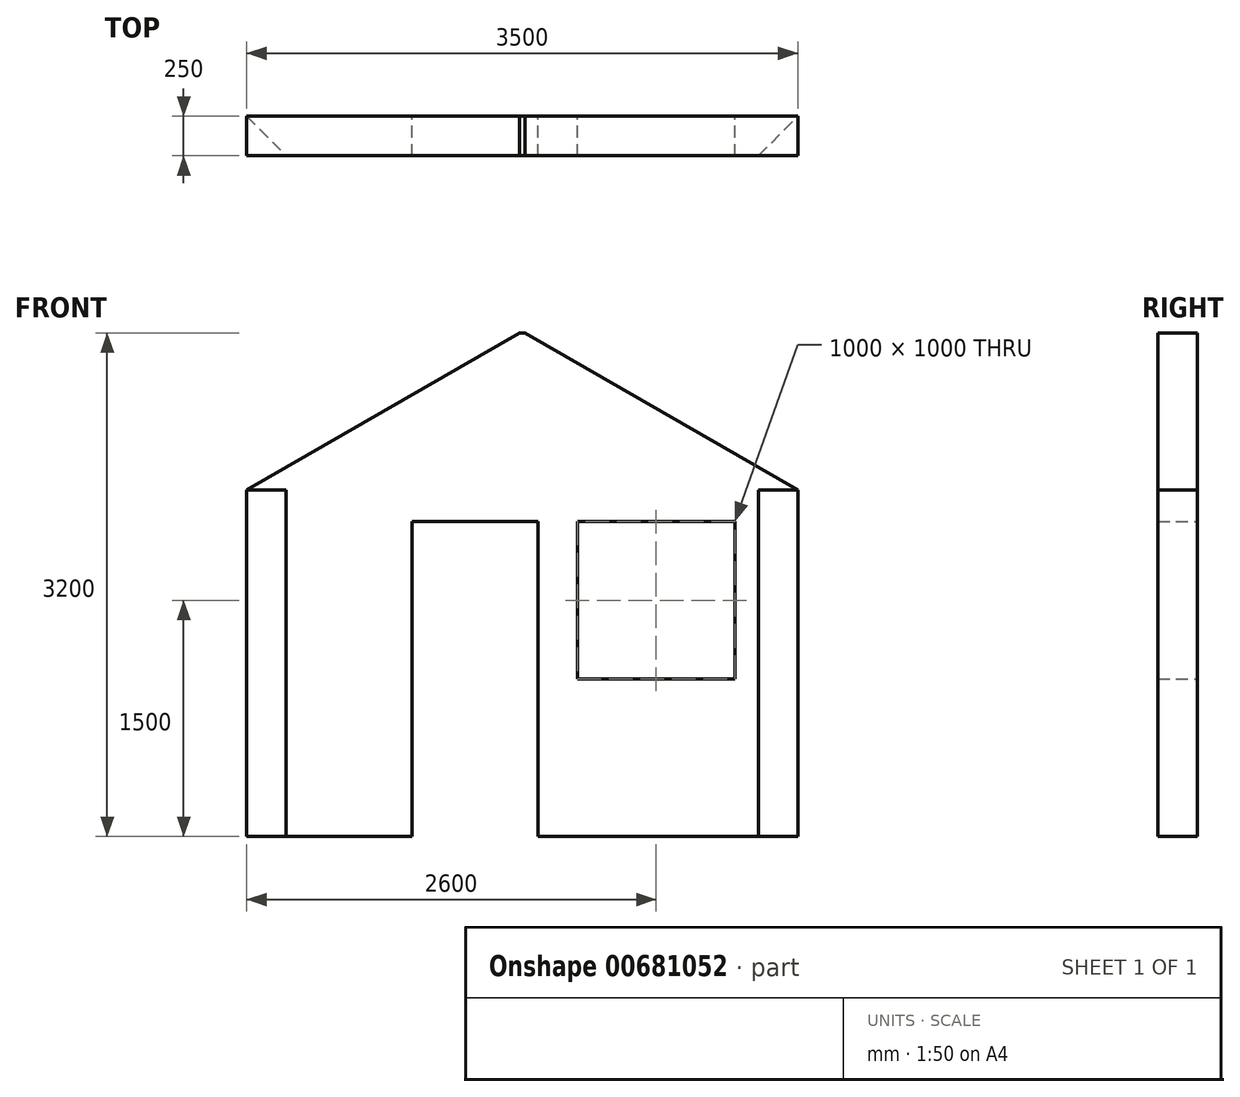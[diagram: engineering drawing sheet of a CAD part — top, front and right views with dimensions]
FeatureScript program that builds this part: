
annotation { "Feature Type Name" : "Feature", "Feature Type Description" : "" }
export const myFeature = defineFeature(function(context is Context, id is Id, definition is map)
    precondition{}
    {
        {
            var Q0;
            Q0=qCreatedBy(makeId("Front.planeOp"),FACE);
            var sketch = newSketch(context, id + "F0", { "sketchPlane" : qUnion([Q0])});
            skLineSegment(sketch, "E0.bottom", {"start": v(0, 0) * mm, "end": v(3500, 0) * mm});
            skLineSegment(sketch, "E0.top", {"start": v(0, 2200) * mm, "end": v(3500, 2200) * mm});
            skLineSegment(sketch, "E0.left", {"start": v(0, 0) * mm, "end": v(0, 2200) * mm});
            skLineSegment(sketch, "E0.right", {"start": v(3500, 0) * mm, "end": v(3500, 2200) * mm});
            skSolve(sketch);
        }
        {
            var Q0;
            Q0=qSketchRegion(id+"F0",true);
            extrude(context, id + "F1", {"entities" : qUnion([Q0]), "depth" : 250 * mm, "offsetDistance" : 25 * mm});
        }
        {
            var Q0;
            Q0=makeQuery(id+"F1.opExtrude","SWEPT_FACE",FACE,{"disambiguationData":[OSD([sQuery(id+"F0.wireOp",EDGE,"E0.top")])]});
            var sketch = newSketch(context, id + "F2", { "sketchPlane" : qUnion([Q0])});
            skLineSegment(sketch, "E1", {"start": v(0, 0) * mm, "end": v(250, -250) * mm});
            skLineSegment(sketch, "E2", {"start": v(250, -250) * mm, "end": v(0, -250) * mm});
            skLineSegment(sketch, "E3", {"start": v(0, -250) * mm, "end": v(0, 0) * mm});
            skLineSegment(sketch, "E4", {"start": v(3500, -250) * mm, "end": v(3250, -250) * mm});
            skLineSegment(sketch, "E5", {"start": v(3250, -250) * mm, "end": v(3500, 0) * mm});
            skLineSegment(sketch, "E6", {"start": v(3500, 0) * mm, "end": v(3500, -250) * mm});
            skLineSegment(sketch, "E7", {"start": v(1750, -250) * mm, "end": v(1750, 0) * mm, "construction": true});
            skSolve(sketch);
        }
        {
            var Q0;
            Q0=qSketchRegion(id+"F2",true);
            extrude(context, id + "F3", {"entities" : qUnion([Q0]), "operationType" : NewBodyOperationType.REMOVE, "endBound" : BoundingType.THROUGH_ALL, "oppositeDirection" : true, "depth" : 25 * mm, "offsetDistance" : 25 * mm});
        }
        {
            var Q0;
            Q0=makeQuery(id+"F1.opExtrude","SWEPT_FACE",FACE,{"disambiguationData":[OSD([sQuery(id+"F0.wireOp",EDGE,"E0.top")])]});
            var sketch = newSketch(context, id + "F4", { "sketchPlane" : qUnion([Q0])});
            skLineSegment(sketch, "E8.bottom", {"start": v(3500, 0) * mm, "end": v(0, 0) * mm});
            skLineSegment(sketch, "E8.top", {"start": v(3500, -250) * mm, "end": v(0, -250) * mm});
            skLineSegment(sketch, "E8.left", {"start": v(3500, 0) * mm, "end": v(3500, -250) * mm});
            skLineSegment(sketch, "E8.right", {"start": v(0, 0) * mm, "end": v(0, -250) * mm});
            skSolve(sketch);
        }
        {
            var Q0;
            Q0=qSketchRegion(id+"F4",true);
            extrude(context, id + "F5", {"entities" : qUnion([Q0]), "operationType" : NewBodyOperationType.ADD, "depth" : 1000 * mm, "offsetDistance" : 25 * mm});
        }
        {
            var Q0;
            Q0=makeQuery(id+"F5.boolean.opBoolean","MERGE",FACE,{"derivedFrom":[makeQuery(id+"F1.opExtrude","CAP_FACE",FACE,{"disambiguationData":[OSD([sQuery(id+"F0.wireOp",EDGE,"E0.bottom"),sQuery(id+"F0.wireOp",EDGE,"E0.top"),sQuery(id+"F0.wireOp",EDGE,"E0.left"),sQuery(id+"F0.wireOp",EDGE,"E0.right")])],"isStart":false}),makeQuery(id+"F5.opExtrude","SWEPT_FACE",FACE,{"disambiguationData":[OSD([sQuery(id+"F4.wireOp",EDGE,"E8.top")])]})]});
            var sketch = newSketch(context, id + "F6", { "sketchPlane" : qUnion([Q0])});
            skLineSegment(sketch, "E9", {"start": v(0, 2200) * mm, "end": v(1750, 3210.36) * mm});
            skLineSegment(sketch, "E10", {"start": v(1750, 3210.36) * mm, "end": v(3500, 2200) * mm});
            skLineSegment(sketch, "E11", {"start": v(3500, 2200) * mm, "end": v(3500, 3200) * mm});
            skLineSegment(sketch, "E12", {"start": v(3500, 3200) * mm, "end": v(0, 3200) * mm});
            skLineSegment(sketch, "E13", {"start": v(0, 3200) * mm, "end": v(0, 2200) * mm});
            skLineSegment(sketch, "E14", {"start": v(1750, 3200) * mm, "end": v(1750, 0) * mm, "construction": true});
            skSolve(sketch);
        }
        {
            var Q0;
            Q0=qSketchRegion(id+"F6",true);
            extrude(context, id + "F7", {"entities" : qUnion([Q0]), "operationType" : NewBodyOperationType.REMOVE, "endBound" : BoundingType.THROUGH_ALL, "oppositeDirection" : true, "depth" : 25 * mm, "offsetDistance" : 25 * mm});
        }
        {
            var Q0;
            Q0=makeQuery(id+"F5.boolean.opBoolean","MERGE",FACE,{"derivedFrom":[makeQuery(id+"F1.opExtrude","CAP_FACE",FACE,{"disambiguationData":[OSD([sQuery(id+"F0.wireOp",EDGE,"E0.bottom"),sQuery(id+"F0.wireOp",EDGE,"E0.top"),sQuery(id+"F0.wireOp",EDGE,"E0.left"),sQuery(id+"F0.wireOp",EDGE,"E0.right")])],"isStart":true}),makeQuery(id+"F5.opExtrude","SWEPT_FACE",FACE,{"disambiguationData":[OSD([sQuery(id+"F4.wireOp",EDGE,"E8.bottom")])]})]});
            var sketch = newSketch(context, id + "F8", { "sketchPlane" : qUnion([Q0])});
            skLineSegment(sketch, "E15.bottom", {"start": v(-1850, 0) * mm, "end": v(-1050, 0) * mm});
            skLineSegment(sketch, "E15.top", {"start": v(-1850, 2000) * mm, "end": v(-1050, 2000) * mm});
            skLineSegment(sketch, "E15.left", {"start": v(-1850, 0) * mm, "end": v(-1850, 2000) * mm});
            skLineSegment(sketch, "E15.right", {"start": v(-1050, 0) * mm, "end": v(-1050, 2000) * mm});
            skSolve(sketch);
        }
        {
            var Q0;
            Q0 = qSketchRegion(id + "F8", true);
            extrude(context, id + "F9", {"entities" : qUnion([Q0]), "operationType" : NewBodyOperationType.REMOVE, "endBound" : BoundingType.THROUGH_ALL, "oppositeDirection" : true, "depth" : 25 * mm, "offsetDistance" : 25 * mm});
        }
        {
            var Q0;
            Q0=makeQuery(id+"F5.boolean.opBoolean","MERGE",FACE,{"derivedFrom":[makeQuery(id+"F1.opExtrude","CAP_FACE",FACE,{"disambiguationData":[OSD([sQuery(id+"F0.wireOp",EDGE,"E0.bottom"),sQuery(id+"F0.wireOp",EDGE,"E0.top"),sQuery(id+"F0.wireOp",EDGE,"E0.left"),sQuery(id+"F0.wireOp",EDGE,"E0.right")])],"isStart":true}),makeQuery(id+"F5.opExtrude","SWEPT_FACE",FACE,{"disambiguationData":[OSD([sQuery(id+"F4.wireOp",EDGE,"E8.bottom")])]})]});
            var sketch = newSketch(context, id + "F10", { "sketchPlane" : qUnion([Q0])});
            skLineSegment(sketch, "E16.bottom", {"start": v(-2100, 2000) * mm, "end": v(-3100, 2000) * mm});
            skLineSegment(sketch, "E16.top", {"start": v(-2100, 1000) * mm, "end": v(-3100, 1000) * mm});
            skLineSegment(sketch, "E16.left", {"start": v(-2100, 2000) * mm, "end": v(-2100, 1000) * mm});
            skLineSegment(sketch, "E16.right", {"start": v(-3100, 2000) * mm, "end": v(-3100, 1000) * mm});
            skSolve(sketch);
        }
        {
            var Q0;
            Q0 = qSketchRegion(id + "F10", true);
            extrude(context, id + "F11", {"entities" : qUnion([Q0]), "operationType" : NewBodyOperationType.REMOVE, "endBound" : BoundingType.THROUGH_ALL, "oppositeDirection" : true, "depth" : 25 * mm, "offsetDistance" : 25 * mm});
        }
    });
